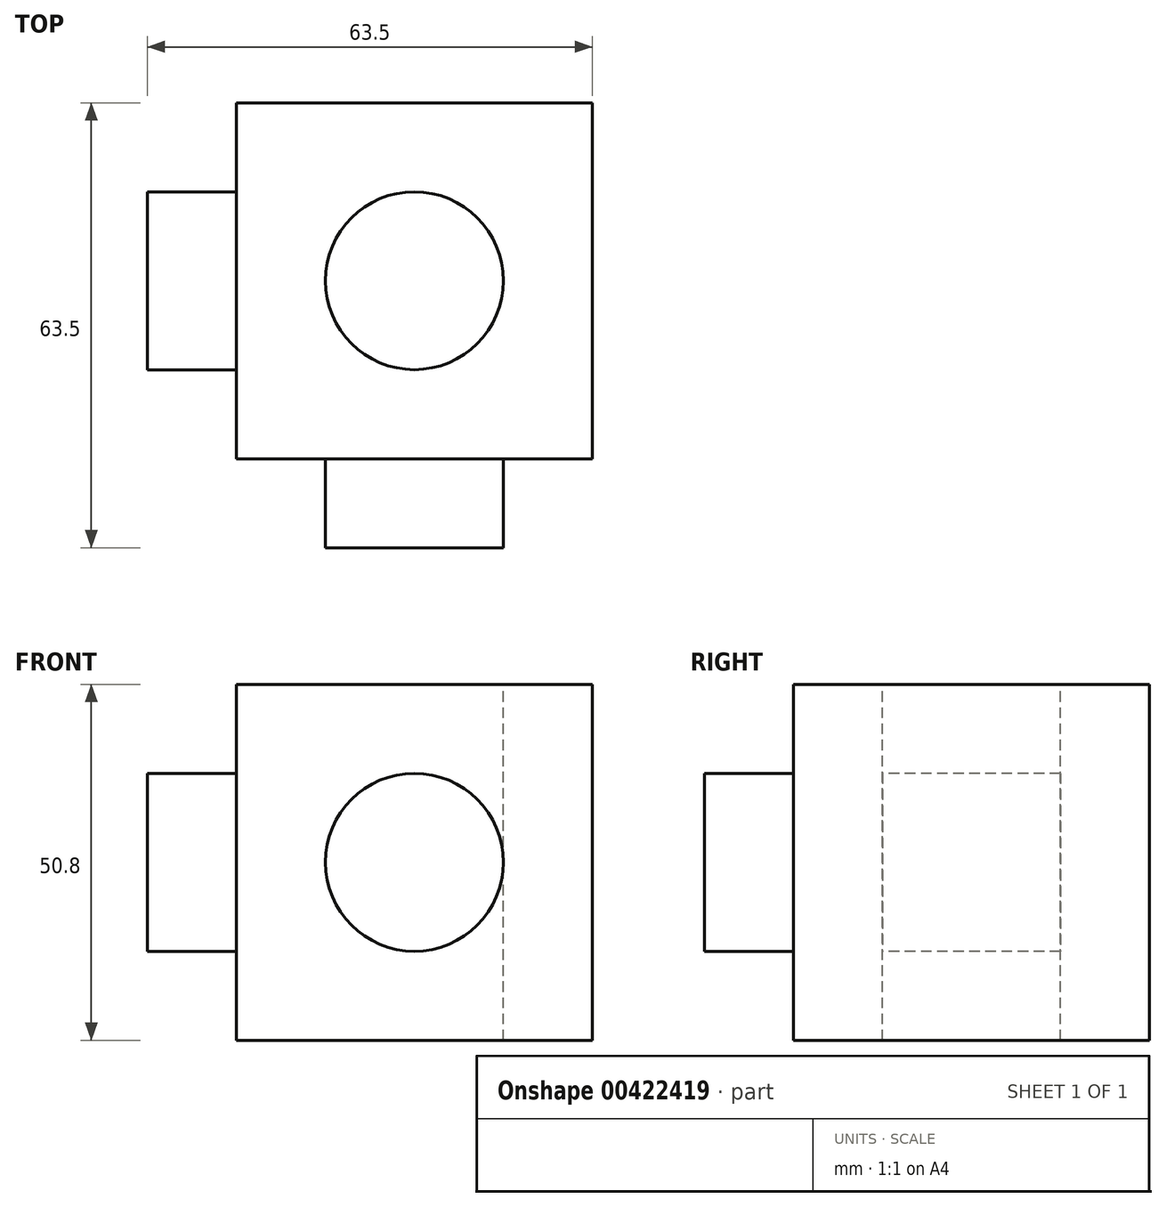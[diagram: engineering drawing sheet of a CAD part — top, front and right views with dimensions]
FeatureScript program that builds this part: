
annotation { "Feature Type Name" : "Feature", "Feature Type Description" : "" }
export const myFeature = defineFeature(function(context is Context, id is Id, definition is map)
    precondition{}
    {
        {
            var Q0;
            Q0=qCreatedBy(makeId("Front.planeOp"),FACE);
            var sketch = newSketch(context, id + "F0", { "sketchPlane" : qUnion([Q0])});
            skLineSegment(sketch, "E0", {"start": v(0, 0) * mm, "end": v(0, 50.8) * mm});
            skLineSegment(sketch, "E1", {"start": v(0, 50.8) * mm, "end": v(50.8, 50.8) * mm});
            skLineSegment(sketch, "E2", {"start": v(50.8, 50.8) * mm, "end": v(50.8, 0) * mm});
            skLineSegment(sketch, "E3", {"start": v(0, 0) * mm, "end": v(50.8, 0) * mm});
            skSolve(sketch);
        }
        {
            var Q0;
            Q0 = qSketchRegion(id + "F0", true);
            extrude(context, id + "F1", {"entities" : qUnion([Q0]), "depth" : 50.8 * mm});
        }
        {
            var Q0;
            Q0=makeQuery(id+"F1.opExtrude","CAP_FACE",FACE,{"disambiguationData":[OSD([sQuery(id+"F0.wireOp",EDGE,"E0"),sQuery(id+"F0.wireOp",EDGE,"E1"),sQuery(id+"F0.wireOp",EDGE,"E2"),sQuery(id+"F0.wireOp",EDGE,"E3")])],"isStart":false});
            var sketch = newSketch(context, id + "F2", { "sketchPlane" : qUnion([Q0])});
            skCircle(sketch, "E4", {"center": v(25.4, 25.4) * mm, "radius": 12.7 * mm});
            skSolve(sketch);
        }
        {
            var Q0;
            Q0=makeQuery(id+"F2.imprint","IMPRINT",FACE,{"disambiguationData":[TD([[makeQuery(id+"F2.imprint","IMPRINT",EDGE,{"derivedFrom":sQuery(id+"F2.wireOp",EDGE,"E4")}),1.0]])]});
            extrude(context, id + "F3", {"entities" : qUnion([Q0]), "operationType" : NewBodyOperationType.ADD, "depth" : 12.7 * mm});
        }
        {
            var Q0;
            Q0=makeQuery(id+"F1.opExtrude","SWEPT_FACE",FACE,{"disambiguationData":[OSD([sQuery(id+"F0.wireOp",EDGE,"E1")])]});
            var sketch = newSketch(context, id + "F4", { "sketchPlane" : qUnion([Q0])});
            skCircle(sketch, "E5", {"center": v(25.4, -25.4) * mm, "radius": 12.7 * mm});
            skSolve(sketch);
        }
        {
            var Q0;
            Q0=makeQuery(id+"F4.imprint","IMPRINT",FACE,{"disambiguationData":[TD([[makeQuery(id+"F4.imprint","IMPRINT",EDGE,{"derivedFrom":sQuery(id+"F4.wireOp",EDGE,"E5")}),1.0]])]});
            extrude(context, id + "F5", {"entities" : qUnion([Q0]), "operationType" : NewBodyOperationType.REMOVE, "oppositeDirection" : true, "depth" : 50.8 * mm});
        }
        {
            var Q0;
            Q0=makeQuery(id+"F1.opExtrude","SWEPT_FACE",FACE,{"disambiguationData":[OSD([sQuery(id+"F0.wireOp",EDGE,"E0")])]});
            var sketch = newSketch(context, id + "F6", { "sketchPlane" : qUnion([Q0])});
            skLineSegment(sketch, "E6.bottom", {"start": v(12.7, 38.1) * mm, "end": v(38.1, 38.1) * mm});
            skLineSegment(sketch, "E6.top", {"start": v(12.7, 12.7) * mm, "end": v(38.1, 12.7) * mm});
            skLineSegment(sketch, "E6.left", {"start": v(12.7, 38.1) * mm, "end": v(12.7, 12.7) * mm});
            skLineSegment(sketch, "E6.right", {"start": v(38.1, 38.1) * mm, "end": v(38.1, 12.7) * mm});
            skSolve(sketch);
        }
        {
            var Q0;
            Q0=makeQuery(id+"F6.imprint","IMPRINT",FACE,{"disambiguationData":[TD([[makeQuery(id+"F6.imprint","IMPRINT",EDGE,{"derivedFrom":sQuery(id+"F6.wireOp",EDGE,"E6.bottom")}),-1.0]])]});
            extrude(context, id + "F7", {"entities" : qUnion([Q0]), "operationType" : NewBodyOperationType.ADD, "depth" : 12.7 * mm});
        }
    });
